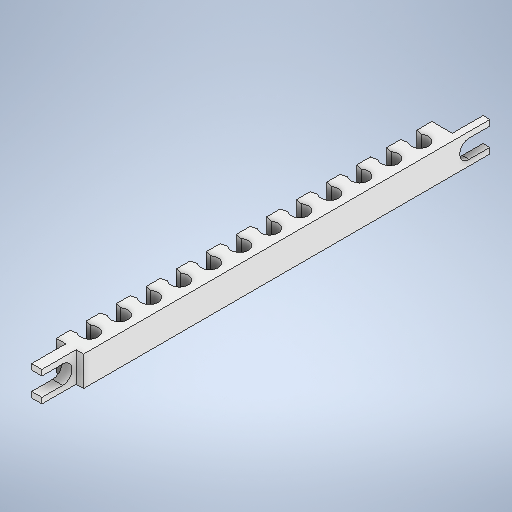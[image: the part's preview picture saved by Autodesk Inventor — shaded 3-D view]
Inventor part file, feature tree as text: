
AUTODESK INVENTOR PART (.ipt)
format: ipt  version: 2025 (Build 290162000, 162)  size: 440,320 bytes
history: native  units: in
note: dims shown in document units (in); Inventor stores cm internally (conversion verified against a paired STEP export)
features: sketch x3, extrude x2
ambient origin geometry x8: Origin, YZ Plane, XZ Plane, XY Plane, X Axis, Y Axis, Z Axis, Center Point
bodies: Solid1 (feature_tree)
feature tree (5):
  extrude  "Extrusion1"  Depth=0.3in
  extrude  "Extrusion2"  Depth=0.125in
  sketch  "Sketch1"  dims[d1=0.3in d5=0.7146in]
  sketch  "Sketch3"  dims[d7=0.125in d8=0.09in]
  sketch  "Sketch Rectangular Pattern5"  dims[d12=0.1in d21=0.4375in d22=0.0in d27=0.5in d28=0.15in d29=0.11in d45=0.4375in d46=0.2188in d47=0.305in d48=0.305in d49=0.27in d50=0.27in d51=0.0in d52=0.0in d66=5.5in d67=2.75in d76=0.4in d77=0.1in d87=0.45in d88=0.1in d89=0.1965in d90=0.1in d91=0.44in d92=4.7244in d94=0.44in d95=0.3937in d97=1.0in]
